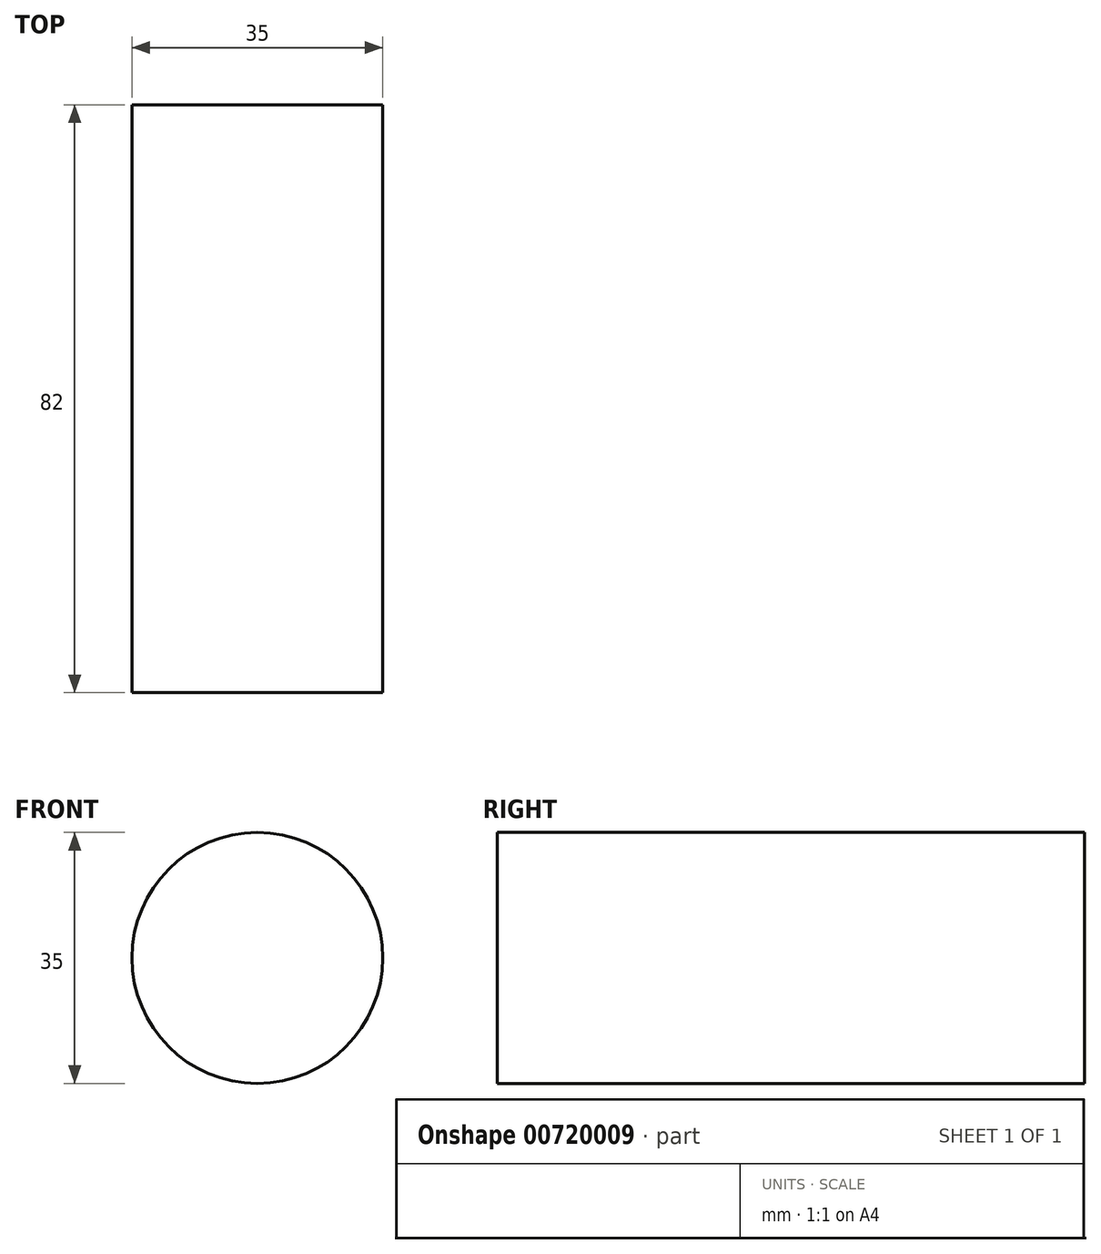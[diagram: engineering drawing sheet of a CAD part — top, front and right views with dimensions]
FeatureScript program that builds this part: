
annotation { "Feature Type Name" : "Feature", "Feature Type Description" : "" }
export const myFeature = defineFeature(function(context is Context, id is Id, definition is map)
    precondition{}
    {
        {
            var Q0;
            Q0=qCreatedBy(makeId("Front.planeOp"),FACE);
            var sketch = newSketch(context, id + "F0", { "sketchPlane" : qUnion([Q0])});
            skCircle(sketch, "E0", {"center": v(0, 0) * mm, "radius": 17.5 * mm});
            skSolve(sketch);
        }
        {
            var Q0;
            Q0=makeQuery(id+"F0.imprint","IMPRINT",FACE,{"disambiguationData":[TD([[makeQuery(id+"F0.imprint","IMPRINT",EDGE,{"derivedFrom":sQuery(id+"F0.wireOp",EDGE,"E0")}),1.0]])]});
            extrude(context, id + "F1", {"entities" : qUnion([Q0]), "depth" : 82 * mm, "offsetDistance" : 25 * mm});
        }
    });
